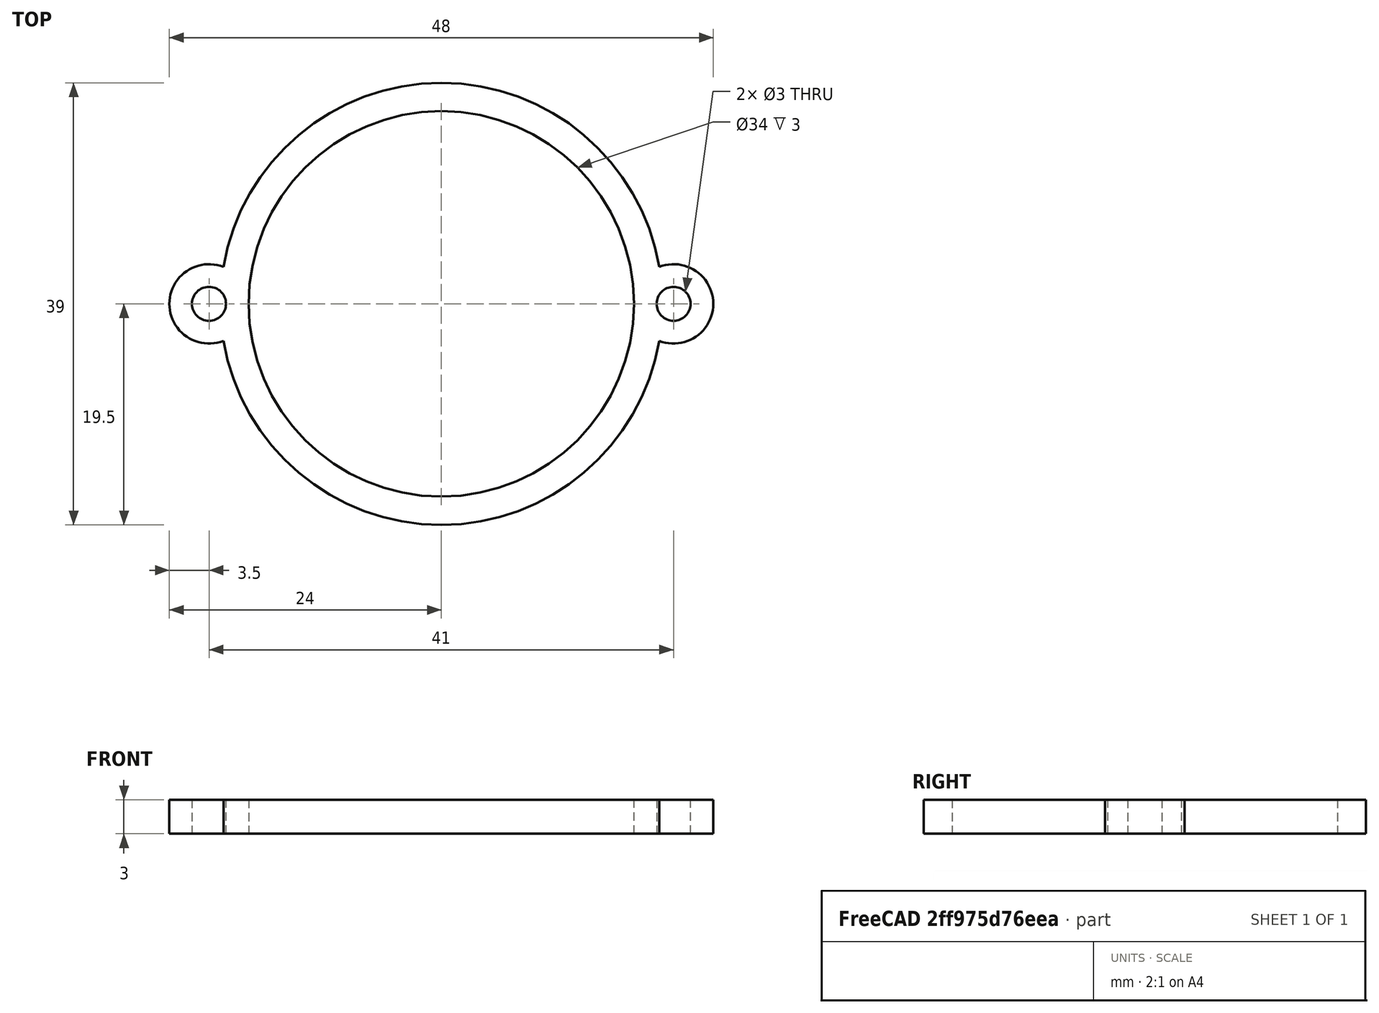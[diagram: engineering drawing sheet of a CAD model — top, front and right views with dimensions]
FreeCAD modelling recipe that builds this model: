
FCSTD DOCUMENT  (FreeCAD 0.19R24276 (Git))
Label: Ring_d31_d34
License: All rights reserved
LicenseURL: http://en.wikipedia.org/wiki/All_rights_reserved
objects: Sketcher::SketchObject×1, PartDesign::Pad×1, PartDesign::Body×1
note: 4 computed .brp shape members not serialized (recipe doc carries the construction recipe); baked Part::Feature solids carry a one-line shape summary decoded from their .brp

FEATURE [Sketcher::SketchObject] Sketch
  FullyConstrained = true
  MapMode = 5
  Support = -> [XY_Plane]
  sketch-geometry (7):
    g0: Circle CenterX=0 CenterY=0 CenterZ=0 NormalX=0 NormalY=0 NormalZ=1 AngleXU=0 Radius=17
    g1: ArcOfCircle CenterX=0 CenterY=0 CenterZ=0 NormalX=0 NormalY=0 NormalZ=1 AngleXU=0 Radius=19.5 StartAngle=0.167955 EndAngle=2.97364
    g2: Circle CenterX=20.5 CenterY=0 CenterZ=0 NormalX=0 NormalY=0 NormalZ=1 AngleXU=0 Radius=1.5
    g3: Circle CenterX=-20.5 CenterY=0 CenterZ=0 NormalX=0 NormalY=0 NormalZ=1 AngleXU=0 Radius=1.5
    g4: ArcOfCircle CenterX=20.5 CenterY=0 CenterZ=0 NormalX=0 NormalY=0 NormalZ=1 AngleXU=0 Radius=3.5 StartAngle=4.33971 EndAngle=8.22666
    g5: ArcOfCircle CenterX=-20.5 CenterY=0 CenterZ=0 NormalX=0 NormalY=0 NormalZ=1 AngleXU=0 Radius=3.5 StartAngle=1.19812 EndAngle=5.08507
    g6: ArcOfCircle CenterX=0 CenterY=0 CenterZ=0 NormalX=0 NormalY=0 NormalZ=1 AngleXU=0 Radius=19.5 StartAngle=3.30955 EndAngle=6.11523
  constraints (19):
    c: Coincident(g0,g-1)
    c: Diameter(g0) = 34
    c: Coincident(g1,g0)
    c: Diameter(g1) = 39
    c: PointOnObject(g2,g-1)
    c: Symmetric(g3,g2,g0)
    c: DistanceX(g3,g2) = 41
    c: Coincident(g4,g2)
    c: Coincident(g5,g3)
    c: Diameter(g4) = 7
    c: Equal(g5,g4)
    c: Diameter(g3) = 3
    c: Equal(g3,g2)
    c: Coincident(g4,g1)
    c: Coincident(g6,g4)
    c: Equal(g1,g6)
    c: Coincident(g1,g6)
    c: Coincident(g5,g6)
    c: Coincident(g5,g1)
FEATURE [PartDesign::Pad] Pad
  Direction = (1,1,1)
  Length = 3
  Length2 = 100
  Profile = -> Sketch
  Type = 0
FEATURE [PartDesign::Body] Body
  Group = -> [Sketch,Pad]
  Origin = -> Origin
  Tip = -> Pad
